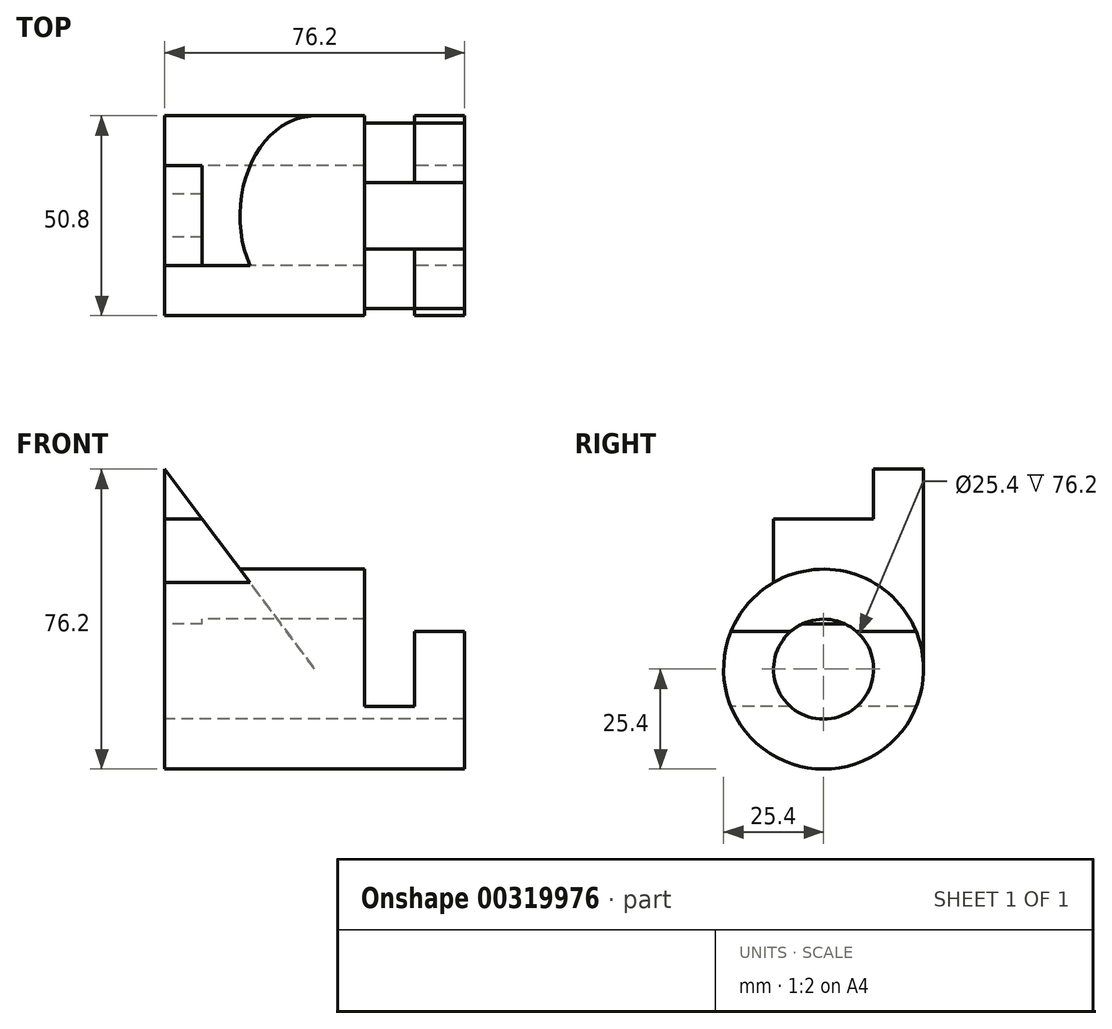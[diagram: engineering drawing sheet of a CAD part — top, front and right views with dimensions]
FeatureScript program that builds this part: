
annotation { "Feature Type Name" : "Feature", "Feature Type Description" : "" }
export const myFeature = defineFeature(function(context is Context, id is Id, definition is map)
    precondition{}
    {
        {
            var Q0;
            Q0=qCreatedBy(makeId("Right.planeOp"),FACE);
            var sketch = newSketch(context, id + "F0", { "sketchPlane" : qUnion([Q0])});
            skCircle(sketch, "E0", {"center": v(0, 0) * mm, "radius": 12.7 * mm});
            skCircle(sketch, "E1", {"center": v(0, 0) * mm, "radius": 25.4 * mm});
            skSolve(sketch);
        }
        {
            var Q0;
            Q0=makeQuery(id+"F0.imprint","IMPRINT",FACE,{"disambiguationData":[TD([[makeQuery(id+"F0.imprint","IMPRINT",EDGE,{"derivedFrom":sQuery(id+"F0.wireOp",EDGE,"E0")}),-1.0]])]});
            extrude(context, id + "F1", {"entities" : qUnion([Q0]), "depth" : 76.2 * mm});
        }
        {
            var Q0;
            Q0=qCreatedBy(makeId("Front.planeOp"),FACE);
            var sketch = newSketch(context, id + "F2", { "sketchPlane" : qUnion([Q0])});
            skLineSegment(sketch, "E2", {"start": v(50.8, 25.4) * mm, "end": v(50.8, -9.52) * mm});
            skLineSegment(sketch, "E3", {"start": v(50.8, -9.52) * mm, "end": v(63.5, -9.52) * mm});
            skLineSegment(sketch, "E4", {"start": v(63.5, -9.52) * mm, "end": v(63.5, 9.53) * mm});
            skLineSegment(sketch, "E5", {"start": v(63.5, 9.53) * mm, "end": v(76.2, 9.53) * mm});
            skLineSegment(sketch, "E6", {"start": v(76.2, 9.53) * mm, "end": v(76.2, 25.4) * mm});
            skLineSegment(sketch, "E7", {"start": v(50.8, 25.4) * mm, "end": v(76.2, 25.4) * mm});
            skLineSegment(sketch, "E8", {"start": v(0, 25.4) * mm, "end": v(76.2, 25.4) * mm});
            skSolve(sketch);
        }
        {
            var Q0;
            {var subQ0=sQuery(id+"F2.wireOp",EDGE,"E2");Q0=makeQuery(id+"F2.imprint","IMPRINT",FACE,{"disambiguationData":[TD([[makeQuery(id+"F2.imprint","IMPRINT",EDGE,{"derivedFrom":subQ0}),1.0]])]});}
            extrude(context, id + "F3", {"entities" : qUnion([Q0]), "operationType" : NewBodyOperationType.REMOVE, "endBound" : BoundingType.SYMMETRIC, "oppositeDirection" : true, "depth" : 55.88 * mm});
        }
        {
            var Q0;
            Q0=qCreatedBy(makeId("Front.planeOp"),FACE);
            cPlane(context, id + "F4", {"entities" : qUnion([Q0]), "cplaneType" : CPlaneType.OFFSET, "offset" : 25.4 * mm, "oppositeDirection" : true, "width" : 152.4 * mm, "height" : 152.4 * mm});
        }
        {
            var Q0;
            Q0=qCreatedBy(id+"F4.planeOp",FACE);
            var sketch = newSketch(context, id + "F5", { "sketchPlane" : qUnion([Q0])});
            skLineSegment(sketch, "E9", {"start": v(38.1, 0) * mm, "end": v(0, 0) * mm});
            skLineSegment(sketch, "E10", {"start": v(0, 0) * mm, "end": v(0, 50.8) * mm});
            skLineSegment(sketch, "E11", {"start": v(0, 50.8) * mm, "end": v(38.1, 0) * mm});
            skSolve(sketch);
        }
        {
            var Q0;
            Q0=makeQuery(id+"F5.imprint","IMPRINT",FACE,{"disambiguationData":[TD([[makeQuery(id+"F5.imprint","IMPRINT",EDGE,{"derivedFrom":sQuery(id+"F5.wireOp",EDGE,"E9")}),-1.0]])]});
            extrude(context, id + "F6", {"entities" : qUnion([Q0]), "operationType" : NewBodyOperationType.ADD, "depth" : 12.7 * mm});
        }
        {
            var Q0;
            Q0=makeQuery(id+"F6.opExtrude","CAP_FACE",FACE,{"disambiguationData":[OSD([sQuery(id+"F5.wireOp",EDGE,"E9"),sQuery(id+"F5.wireOp",EDGE,"E10"),sQuery(id+"F5.wireOp",EDGE,"E11")])],"isStart":false});
            var sketch = newSketch(context, id + "F7", { "sketchPlane" : qUnion([Q0])});
            skLineSegment(sketch, "E12.bottom", {"start": v(0, 38.1) * mm, "end": v(9.53, 38.1) * mm});
            skLineSegment(sketch, "E12.top", {"start": v(0, 11.47) * mm, "end": v(9.53, 11.47) * mm});
            skLineSegment(sketch, "E12.left", {"start": v(0, 38.1) * mm, "end": v(0, 11.47) * mm});
            skLineSegment(sketch, "E12.right", {"start": v(9.53, 38.1) * mm, "end": v(9.53, 11.47) * mm});
            skSolve(sketch);
        }
        {
            var Q0;
            {var subQ0=sQuery(id+"F7.wireOp",EDGE,"E12.top");Q0=makeQuery(id+"F7.imprint","IMPRINT",FACE,{"disambiguationData":[TD([[makeQuery(id+"F7.imprint","IMPRINT",EDGE,{"derivedFrom":subQ0}),1.0]])]});}
            var Q1;
            {var subQ0=sQuery(id+"F7.wireOp",EDGE,"E12.right");var subQ1=sQuery(id+"F5.wireOp",EDGE,"E11");var subQ2=makeQuery(id+"F6.opExtrude","CAP_EDGE",EDGE,{"disambiguationData":[OSD([subQ1])],"isStart":false});var subQ3=makeQuery(id+"F7.imprint","INTERSECT",VERTEX,{"derivedFrom":[subQ2,sQuery(id+"F7.wireOp",EDGE,"E12.bottom"),subQ0]});Q1=makeQuery(id+"F7.imprint","IMPRINT",FACE,{"disambiguationData":[TD([[makeQuery(id+"F7.imprint","IMPRINT",EDGE,{"disambiguationData":[TD([[subQ3,-1.0]])],"derivedFrom":subQ0}),1.0]])]});}
            var Q2;
            {var subQ0=sQuery(id+"F7.wireOp",EDGE,"E12.bottom");Q2=makeQuery(id+"F7.imprint","IMPRINT",FACE,{"disambiguationData":[TD([[makeQuery(id+"F7.imprint","IMPRINT",EDGE,{"derivedFrom":subQ0}),-1.0]])]});}
            extrude(context, id + "F8", {"entities" : qUnion([Q0, Q1, Q2]), "operationType" : NewBodyOperationType.ADD, "depth" : 25.4 * mm});
        }
    });
